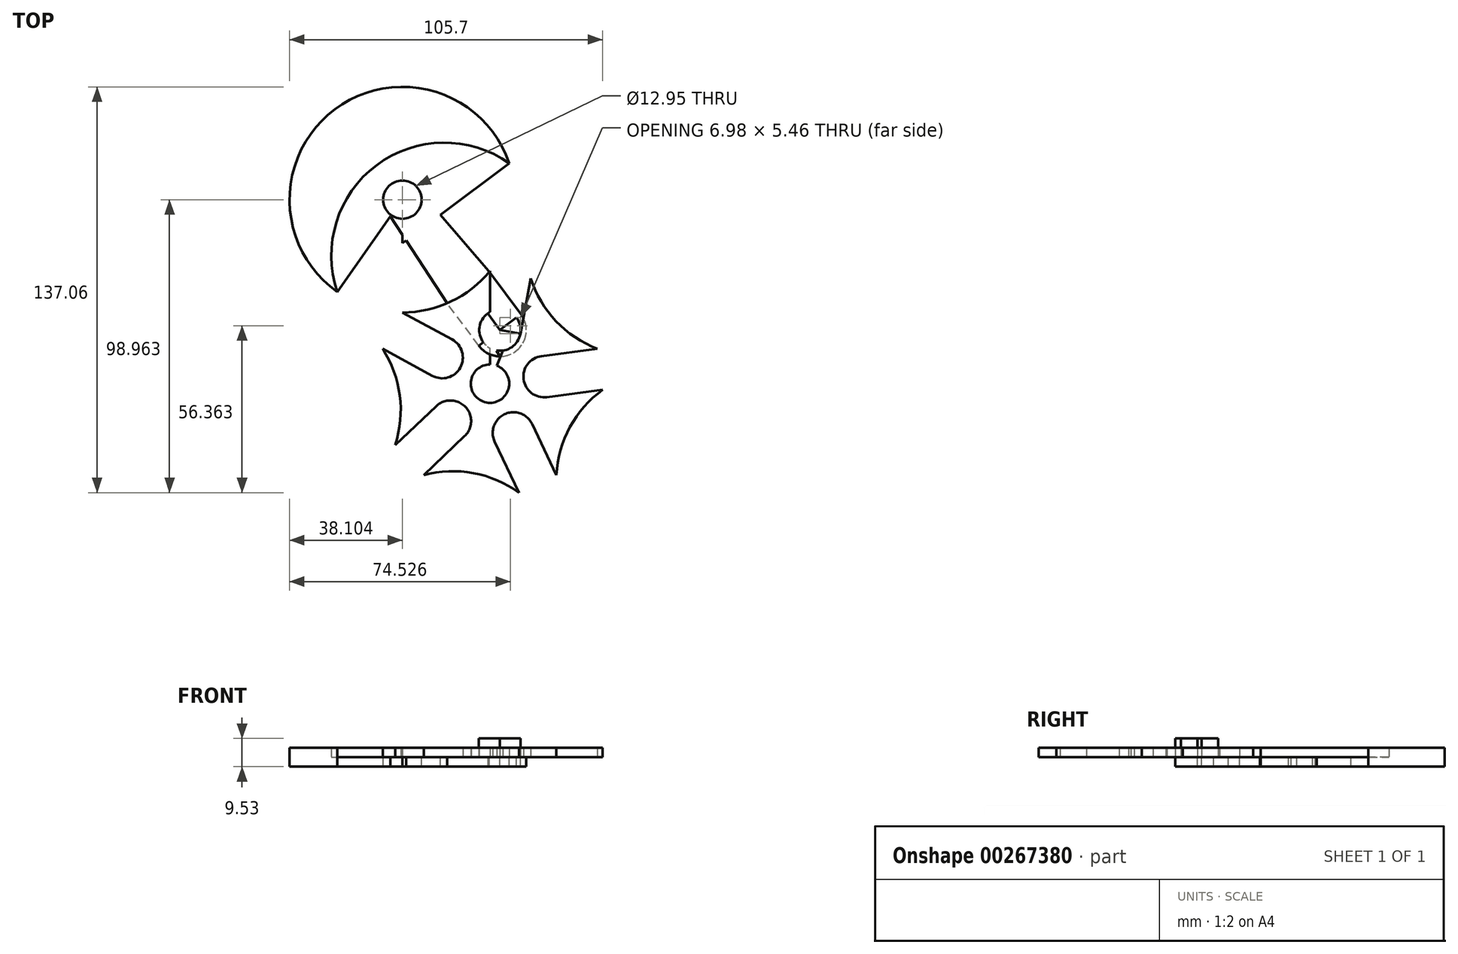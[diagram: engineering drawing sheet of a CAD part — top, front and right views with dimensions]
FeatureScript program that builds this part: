
annotation { "Feature Type Name" : "Feature", "Feature Type Description" : "" }
export const myFeature = defineFeature(function(context is Context, id is Id, definition is map)
    precondition{}
    {
        {
            var Q0;
            Q0=qCreatedBy(makeId("Top.planeOp"),FACE);
            var sketch = newSketch(context, id + "F0", { "sketchPlane" : qUnion([Q0])});
            skCircle(sketch, "E0", {"center": v(0, 0) * mm, "radius": 38.1 * mm});
            skLineSegment(sketch, "E1", {"start": v(0, 0) * mm, "end": v(0, 38.1) * mm});
            skLineSegment(sketch, "E2", {"start": v(0, 0) * mm, "end": v(-36.24, 11.77) * mm});
            skLineSegment(sketch, "E3", {"start": v(0, 0) * mm, "end": v(-22.4, -30.82) * mm});
            skLineSegment(sketch, "E4", {"start": v(-22.4, -30.82) * mm, "end": v(-32, -20.68) * mm});
            skLineSegment(sketch, "E5", {"start": v(-32, -20.68) * mm, "end": v(-18.17, -7.58) * mm});
            skLineSegment(sketch, "E6", {"start": v(-18.17, -7.58) * mm, "end": v(-8.56, -17.73) * mm});
            skLineSegment(sketch, "E7", {"start": v(-8.56, -17.73) * mm, "end": v(-22.4, -30.82) * mm});
            skCircle(sketch, "E8", {"center": v(-13.36, -12.65) * mm, "radius": 6.99 * mm});
            skLineSegment(sketch, "E9", {"start": v(-32, -20.68) * mm, "end": v(-36.24, 11.77) * mm});
            skArc(sketch, "E10.MirrorC", {"start": v(-36.24, 11.77) * mm, "mid": v(-30.46, -3.97) * mm, "end": v(-32, -20.68) * mm});
            skLineSegment(sketch, "E11", {"start": v(0, 0) * mm, "end": v(22.4, -30.82) * mm});
            skLineSegment(sketch, "E12", {"start": v(22.4, -30.82) * mm, "end": v(0, 0) * mm});
            skLineSegment(sketch, "E13", {"start": v(0, 0) * mm, "end": v(36.24, 11.77) * mm});
            skLineSegment(sketch, "E14", {"start": v(22.4, -30.82) * mm, "end": v(9.78, -36.82) * mm});
            skLineSegment(sketch, "E15", {"start": v(9.78, -36.82) * mm, "end": v(1.6, -19.62) * mm});
            skLineSegment(sketch, "E16", {"start": v(1.6, -19.62) * mm, "end": v(14.21, -13.62) * mm});
            skLineSegment(sketch, "E17", {"start": v(14.21, -13.62) * mm, "end": v(22.4, -30.82) * mm});
            skCircle(sketch, "E18", {"center": v(7.9, -16.62) * mm, "radius": 6.99 * mm});
            skPoint(sketch, "E19.trimOffspring.end.orphan", {"position": v(-7.55, 17.26) * mm});
            skPoint(sketch, "E20.center.orphan", {"position": v(-1.29, 18.31) * mm});
            skPoint(sketch, "E20.start.orphan", {"position": v(4.97, 19.37) * mm});
            skLineSegment(sketch, "E21", {"start": v(-36.24, 11.77) * mm, "end": v(-29.56, 24.04) * mm});
            skLineSegment(sketch, "E22", {"start": v(-29.56, 24.04) * mm, "end": v(-12.82, 14.93) * mm});
            skLineSegment(sketch, "E23", {"start": v(-29.56, 24.04) * mm, "end": v(0, 38.1) * mm});
            skArc(sketch, "E24.MirrorC", {"start": v(0, 38.1) * mm, "mid": v(-13.2, 27.74) * mm, "end": v(-29.56, 24.04) * mm});
            skLineSegment(sketch, "E25", {"start": v(0, 38.1) * mm, "end": v(13.73, 35.54) * mm});
            skLineSegment(sketch, "E26", {"start": v(13.73, 35.54) * mm, "end": v(0, 0) * mm});
            skLineSegment(sketch, "E27", {"start": v(13.73, 35.54) * mm, "end": v(10.24, 16.81) * mm});
            skLineSegment(sketch, "E28", {"start": v(10.24, 16.81) * mm, "end": v(-3.5, 19.37) * mm});
            skLineSegment(sketch, "E29", {"start": v(-3.5, 19.37) * mm, "end": v(0, 38.1) * mm});
            skCircle(sketch, "E30", {"center": v(3.37, 18.1) * mm, "radius": 6.99 * mm});
            skLineSegment(sketch, "E31", {"start": v(13.73, 35.54) * mm, "end": v(36.24, 11.77) * mm});
            skArc(sketch, "E32.MirrorC", {"start": v(36.24, 11.77) * mm, "mid": v(22.3, 21.12) * mm, "end": v(13.73, 35.54) * mm});
            skLineSegment(sketch, "E33", {"start": v(36.24, 11.77) * mm, "end": v(38.04, -2.08) * mm});
            skLineSegment(sketch, "E34", {"start": v(38.04, -2.08) * mm, "end": v(19.15, -4.54) * mm});
            skLineSegment(sketch, "E35", {"start": v(19.15, -4.54) * mm, "end": v(17.35, 9.3) * mm});
            skLineSegment(sketch, "E36", {"start": v(17.35, 9.3) * mm, "end": v(36.24, 11.77) * mm});
            skLineSegment(sketch, "E37", {"start": v(38.04, -2.08) * mm, "end": v(22.4, -30.82) * mm});
            skArc(sketch, "E38.MirrorC", {"start": v(22.4, -30.82) * mm, "mid": v(26.98, -14.69) * mm, "end": v(38.04, -2.08) * mm});
            skCircle(sketch, "E39", {"center": v(18.25, 2.38) * mm, "radius": 6.99 * mm});
            skLineSegment(sketch, "E40", {"start": v(-22.4, -30.82) * mm, "end": v(9.78, -36.82) * mm});
            skArc(sketch, "E41.MirrorC", {"start": v(-22.4, -30.82) * mm, "mid": v(-5.63, -30.2) * mm, "end": v(9.78, -36.82) * mm});
            skLineSegment(sketch, "E42", {"start": v(-36.24, 11.77) * mm, "end": v(-19.5, 2.66) * mm});
            skLineSegment(sketch, "E43", {"start": v(-12.82, 14.93) * mm, "end": v(-19.5, 2.66) * mm});
            skCircle(sketch, "E44", {"center": v(-16.16, 8.8) * mm, "radius": 6.99 * mm});
            skSolve(sketch);
        }
        {
            var Q0;
            {var subQ0=sQuery(id+"F0.wireOp",EDGE,"E22");Q0=makeQuery(id+"F0.imprint","IMPRINT",FACE,{"disambiguationData":[TD([[makeQuery(id+"F0.imprint","IMPRINT",EDGE,{"derivedFrom":subQ0}),1.0]])]});}
            var Q1;
            {var subQ0=sQuery(id+"F0.wireOp",EDGE,"E5");Q1=makeQuery(id+"F0.imprint","IMPRINT",FACE,{"disambiguationData":[TD([[makeQuery(id+"F0.imprint","IMPRINT",EDGE,{"derivedFrom":subQ0}),1.0]])]});}
            var Q2;
            {var subQ1=sQuery(id+"F0.wireOp",EDGE,"E7");Q2=makeQuery(id+"F0.imprint","IMPRINT",FACE,{"disambiguationData":[TD([[makeQuery(id+"F0.imprint","IMPRINT",EDGE,{"derivedFrom":subQ1}),1.0]])]});}
            var Q3;
            {var subQ1=sQuery(id+"F0.wireOp",EDGE,"E17");Q3=makeQuery(id+"F0.imprint","IMPRINT",FACE,{"disambiguationData":[TD([[makeQuery(id+"F0.imprint","IMPRINT",EDGE,{"derivedFrom":subQ1}),1.0]])]});}
            var Q4;
            {var subQ1=sQuery(id+"F0.wireOp",EDGE,"E27");Q4=makeQuery(id+"F0.imprint","IMPRINT",FACE,{"disambiguationData":[TD([[makeQuery(id+"F0.imprint","IMPRINT",EDGE,{"derivedFrom":subQ1}),1.0]])]});}
            var Q5;
            {var subQ1=sQuery(id+"F0.wireOp",EDGE,"E1");var subQ3=sQuery(id+"F0.wireOp",EDGE,"E30");var subQ4=makeQuery(id+"F0.imprint","INTERSECT",VERTEX,{"disambiguationData":[OD(0.0)],"derivedFrom":[subQ1,subQ3]});Q5=makeQuery(id+"F0.imprint","IMPRINT",FACE,{"disambiguationData":[TD([[makeQuery(id+"F0.imprint","IMPRINT",EDGE,{"disambiguationData":[TD([[subQ4,-1.0]])],"derivedFrom":subQ3}),-1.0]])]});}
            extrude(context, id + "F1", {"entities" : qUnion([Q0, Q1, Q2, Q3, Q4, Q5]), "depth" : 3.17 * mm});
        }
        {
            var Q0;
            Q0=qCreatedBy(makeId("Top.planeOp"),FACE);
            var sketch = newSketch(context, id + "F2", { "sketchPlane" : qUnion([Q0])});
            skCircle(sketch, "E45", {"center": v(0, 0) * mm, "radius": 38.1 * mm});
            skLineSegment(sketch, "E46", {"start": v(0, 38.1) * mm, "end": v(0, 0) * mm});
            skLineSegment(sketch, "E47", {"start": v(0, 38.1) * mm, "end": v(13.73, 35.54) * mm});
            skLineSegment(sketch, "E48", {"start": v(0, 38.1) * mm, "end": v(-3.5, 19.37) * mm});
            skLineSegment(sketch, "E49", {"start": v(13.73, 35.54) * mm, "end": v(10.24, 16.81) * mm});
            skLineSegment(sketch, "E50", {"start": v(10.24, 16.81) * mm, "end": v(-3.5, 19.37) * mm});
            skCircle(sketch, "E51", {"center": v(3.37, 18.1) * mm, "radius": 6.99 * mm});
            skLineSegment(sketch, "E52", {"start": v(0, 0) * mm, "end": v(-36.24, 11.77) * mm});
            skLineSegment(sketch, "E53", {"start": v(0, 0) * mm, "end": v(-29.56, 24.04) * mm});
            skLineSegment(sketch, "E54", {"start": v(-29.56, 24.04) * mm, "end": v(-36.24, 11.77) * mm});
            skLineSegment(sketch, "E55", {"start": v(0, 38.1) * mm, "end": v(-29.56, 24.04) * mm});
            skCircle(sketch, "E56.MirrorC", {"center": v(-29.56, 62.14) * mm, "radius": 38.1 * mm});
            skCircle(sketch, "E57", {"center": v(3.37, 18.1) * mm, "radius": 8.9 * mm});
            skLineSegment(sketch, "E58", {"start": v(3.37, 18.1) * mm, "end": v(-25.68, 56.96) * mm});
            skLineSegment(sketch, "E59", {"start": v(3.37, 18.1) * mm, "end": v(10.5, 23.42) * mm});
            skLineSegment(sketch, "E60", {"start": v(10.5, 23.42) * mm, "end": v(-3.75, 12.77) * mm});
            skLineSegment(sketch, "E61", {"start": v(-3.75, 12.77) * mm, "end": v(-14.5, 27.15) * mm});
            skLineSegment(sketch, "E62", {"start": v(10.5, 23.42) * mm, "end": v(-0.25, 37.8) * mm});
            skCircle(sketch, "E63", {"center": v(-29.56, 62.14) * mm, "radius": 6.48 * mm});
            skLineSegment(sketch, "E64", {"start": v(-0.25, 37.8) * mm, "end": v(-24.63, 66.35) * mm});
            skLineSegment(sketch, "E65", {"start": v(-14.5, 27.15) * mm, "end": v(-34.98, 58.6) * mm});
            skLineSegment(sketch, "E66", {"start": v(-34.98, 58.6) * mm, "end": v(-24.63, 66.35) * mm});
            skLineSegment(sketch, "E67", {"start": v(-29.56, 24.04) * mm, "end": v(-29.56, 62.14) * mm});
            skLineSegment(sketch, "E68", {"start": v(-29.56, 62.14) * mm, "end": v(6.52, 74.4) * mm});
            skLineSegment(sketch, "E69", {"start": v(-29.56, 62.14) * mm, "end": v(-51.53, 31.02) * mm});
            skLineSegment(sketch, "E70.trimOffspring", {"start": v(-0.62, 38.1) * mm, "end": v(-0.25, 37.8) * mm});
            skLineSegment(sketch, "E71", {"start": v(-25.68, 56.96) * mm, "end": v(-29.56, 62.14) * mm});
            skLineSegment(sketch, "E72", {"start": v(-51.53, 31.02) * mm, "end": v(6.52, 74.4) * mm});
            skArc(sketch, "E73.MirrorC", {"start": v(6.52, 74.4) * mm, "mid": v(-38.27, 73.8) * mm, "end": v(-51.53, 31.02) * mm});
            skLineSegment(sketch, "E74", {"start": v(-10.7, 33.01) * mm, "end": v(10.8, -3.44) * mm});
            skSolve(sketch);
        }
        {
            var Q0;
            {var subQ0=sQuery(id+"F2.wireOp",EDGE,"E51");var subQ1=sQuery(id+"F2.wireOp",EDGE,"E46");var subQ2=makeQuery(id+"F2.imprint","INTERSECT",VERTEX,{"disambiguationData":[OD(0.0)],"derivedFrom":[subQ1,subQ0]});Q0=makeQuery(id+"F2.imprint","IMPRINT",FACE,{"disambiguationData":[TD([[makeQuery(id+"F2.imprint","IMPRINT",EDGE,{"disambiguationData":[TD([[subQ2,-1.0]])],"derivedFrom":subQ1}),1.0]])]});}
            var Q1;
            {var subQ0=sQuery(id+"F2.wireOp",EDGE,"E51");var subQ3=sQuery(id+"F2.wireOp",EDGE,"E60");var subQ5=makeQuery(id+"F2.imprint","INTERSECT",VERTEX,{"disambiguationData":[OD(0.0)],"derivedFrom":[subQ0,subQ3]});Q1=makeQuery(id+"F2.imprint","IMPRINT",FACE,{"disambiguationData":[TD([[makeQuery(id+"F2.imprint","IMPRINT",EDGE,{"disambiguationData":[TD([[subQ5,1.0]])],"derivedFrom":subQ0}),1.0]])]});}
            var Q2;
            {var subQ0=sQuery(id+"F2.wireOp",EDGE,"E60");var subQ1=sQuery(id+"F2.wireOp",EDGE,"E46");var subQ2=makeQuery(id+"F2.imprint","INTERSECT",VERTEX,{"derivedFrom":[subQ1,subQ0]});Q2=makeQuery(id+"F2.imprint","IMPRINT",FACE,{"disambiguationData":[TD([[makeQuery(id+"F2.imprint","IMPRINT",EDGE,{"disambiguationData":[TD([[subQ2,-1.0]])],"derivedFrom":subQ1}),1.0]])]});}
            var Q3;
            {var subQ0=sQuery(id+"F2.wireOp",EDGE,"E50");var subQ1=sQuery(id+"F2.wireOp",EDGE,"E46");var subQ2=makeQuery(id+"F2.imprint","INTERSECT",VERTEX,{"derivedFrom":[subQ1,subQ0]});Q3=makeQuery(id+"F2.imprint","IMPRINT",FACE,{"disambiguationData":[TD([[makeQuery(id+"F2.imprint","IMPRINT",EDGE,{"disambiguationData":[TD([[subQ2,-1.0]])],"derivedFrom":subQ1}),-1.0]])]});}
            var Q4;
            {var subQ0=sQuery(id+"F2.wireOp",EDGE,"E50");var subQ1=sQuery(id+"F2.wireOp",EDGE,"E46");var subQ2=makeQuery(id+"F2.imprint","INTERSECT",VERTEX,{"derivedFrom":[subQ1,subQ0]});Q4=makeQuery(id+"F2.imprint","IMPRINT",FACE,{"disambiguationData":[TD([[makeQuery(id+"F2.imprint","IMPRINT",EDGE,{"disambiguationData":[TD([[subQ2,-1.0]])],"derivedFrom":subQ1}),1.0]])]});}
            var Q5;
            {var subQ0=sQuery(id+"F2.wireOp",EDGE,"E58");var subQ1=sQuery(id+"F2.wireOp",EDGE,"E46");var subQ2=makeQuery(id+"F2.imprint","INTERSECT",VERTEX,{"derivedFrom":[subQ1,subQ0]});Q5=makeQuery(id+"F2.imprint","IMPRINT",FACE,{"disambiguationData":[TD([[makeQuery(id+"F2.imprint","IMPRINT",EDGE,{"disambiguationData":[TD([[subQ2,-1.0]])],"derivedFrom":subQ1}),1.0]])]});}
            var Q6;
            {var subQ0=sQuery(id+"F2.wireOp",EDGE,"E51");var subQ1=sQuery(id+"F2.wireOp",EDGE,"E46");var subQ2=makeQuery(id+"F2.imprint","INTERSECT",VERTEX,{"disambiguationData":[OD(1.0)],"derivedFrom":[subQ1,subQ0]});Q6=makeQuery(id+"F2.imprint","IMPRINT",FACE,{"disambiguationData":[TD([[makeQuery(id+"F2.imprint","IMPRINT",EDGE,{"disambiguationData":[TD([[subQ2,-1.0]])],"derivedFrom":subQ1}),-1.0]])]});}
            var Q7;
            {var subQ1=sQuery(id+"F2.wireOp",EDGE,"E48");var subQ3=sQuery(id+"F2.wireOp",EDGE,"E57");var subQ4=makeQuery(id+"F2.imprint","INTERSECT",VERTEX,{"derivedFrom":[subQ1,subQ3]});Q7=makeQuery(id+"F2.imprint","IMPRINT",FACE,{"disambiguationData":[TD([[makeQuery(id+"F2.imprint","IMPRINT",EDGE,{"disambiguationData":[TD([[subQ4,-1.0]])],"derivedFrom":subQ1}),-1.0]])]});}
            var Q8;
            {var subQ0=sQuery(id+"F2.wireOp",EDGE,"E51");var subQ1=sQuery(id+"F2.wireOp",EDGE,"E46");var subQ2=makeQuery(id+"F2.imprint","INTERSECT",VERTEX,{"disambiguationData":[OD(1.0)],"derivedFrom":[subQ1,subQ0]});Q8=makeQuery(id+"F2.imprint","IMPRINT",FACE,{"disambiguationData":[TD([[makeQuery(id+"F2.imprint","IMPRINT",EDGE,{"disambiguationData":[TD([[subQ2,-1.0]])],"derivedFrom":subQ1}),1.0]])]});}
            var Q9;
            {var subQ1=sQuery(id+"F2.wireOp",EDGE,"E49");var subQ3=sQuery(id+"F2.wireOp",EDGE,"E57");var subQ4=makeQuery(id+"F2.imprint","INTERSECT",VERTEX,{"derivedFrom":[subQ1,subQ3]});Q9=makeQuery(id+"F2.imprint","IMPRINT",FACE,{"disambiguationData":[TD([[makeQuery(id+"F2.imprint","IMPRINT",EDGE,{"disambiguationData":[TD([[subQ4,-1.0]])],"derivedFrom":subQ1}),-1.0]])]});}
            var Q10;
            {var subQ0=sQuery(id+"F2.wireOp",EDGE,"E57");var subQ1=sQuery(id+"F2.wireOp",EDGE,"E46");var subQ2=makeQuery(id+"F2.imprint","INTERSECT",VERTEX,{"disambiguationData":[OD(0.0)],"derivedFrom":[subQ1,subQ0]});Q10=makeQuery(id+"F2.imprint","IMPRINT",FACE,{"disambiguationData":[TD([[makeQuery(id+"F2.imprint","IMPRINT",EDGE,{"disambiguationData":[TD([[subQ2,-1.0]])],"derivedFrom":subQ1}),1.0]])]});}
            var Q11;
            {var subQ0=sQuery(id+"F2.wireOp",EDGE,"E57");var subQ1=sQuery(id+"F2.wireOp",EDGE,"E46");var subQ2=makeQuery(id+"F2.imprint","INTERSECT",VERTEX,{"disambiguationData":[OD(0.0)],"derivedFrom":[subQ1,subQ0]});Q11=makeQuery(id+"F2.imprint","IMPRINT",FACE,{"disambiguationData":[TD([[makeQuery(id+"F2.imprint","IMPRINT",EDGE,{"disambiguationData":[TD([[subQ2,-1.0]])],"derivedFrom":subQ1}),-1.0]])]});}
            var Q12;
            {var subQ1=sQuery(id+"F2.wireOp",EDGE,"E48");var subQ3=sQuery(id+"F2.wireOp",EDGE,"E57");var subQ4=makeQuery(id+"F2.imprint","INTERSECT",VERTEX,{"derivedFrom":[subQ1,subQ3]});Q12=makeQuery(id+"F2.imprint","IMPRINT",FACE,{"disambiguationData":[TD([[makeQuery(id+"F2.imprint","IMPRINT",EDGE,{"disambiguationData":[TD([[subQ4,1.0]])],"derivedFrom":subQ3}),1.0]])]});}
            var Q13;
            {var subQ0=sQuery(id+"F2.wireOp",EDGE,"E61");Q13=makeQuery(id+"F2.imprint","IMPRINT",FACE,{"disambiguationData":[TD([[makeQuery(id+"F2.imprint","IMPRINT",EDGE,{"derivedFrom":subQ0}),-1.0]])]});}
            var Q14;
            {var subQ0=sQuery(id+"F2.wireOp",EDGE,"E62");var subQ1=sQuery(id+"F2.wireOp",EDGE,"E48");var subQ2=makeQuery(id+"F2.imprint","INTERSECT",VERTEX,{"derivedFrom":[subQ1,subQ0]});Q14=makeQuery(id+"F2.imprint","IMPRINT",FACE,{"disambiguationData":[TD([[makeQuery(id+"F2.imprint","IMPRINT",EDGE,{"disambiguationData":[TD([[subQ2,-1.0]])],"derivedFrom":subQ1}),-1.0]])]});}
            var Q15;
            {var subQ0=sQuery(id+"F2.wireOp",EDGE,"E62");var subQ1=sQuery(id+"F2.wireOp",EDGE,"E46");var subQ2=makeQuery(id+"F2.imprint","INTERSECT",VERTEX,{"derivedFrom":[subQ1,subQ0]});Q15=makeQuery(id+"F2.imprint","IMPRINT",FACE,{"disambiguationData":[TD([[makeQuery(id+"F2.imprint","IMPRINT",EDGE,{"disambiguationData":[TD([[subQ2,-1.0]])],"derivedFrom":subQ1}),1.0]])]});}
            var Q16;
            {var subQ5=sQuery(id+"F2.wireOp",EDGE,"E46");var subQ7=sQuery(id+"F2.wireOp",EDGE,"E62");var subQ8=makeQuery(id+"F2.imprint","INTERSECT",VERTEX,{"derivedFrom":[subQ5,subQ7]});Q16=makeQuery(id+"F2.imprint","IMPRINT",FACE,{"disambiguationData":[TD([[makeQuery(id+"F2.imprint","IMPRINT",EDGE,{"disambiguationData":[TD([[subQ8,-1.0]])],"derivedFrom":subQ5}),-1.0]])]});}
            var Q17;
            {var subQ0=sQuery(id+"F2.wireOp",EDGE,"E51");var subQ1=sQuery(id+"F2.wireOp",EDGE,"E46");var subQ2=makeQuery(id+"F2.imprint","INTERSECT",VERTEX,{"disambiguationData":[OD(0.0)],"derivedFrom":[subQ1,subQ0]});Q17=makeQuery(id+"F2.imprint","IMPRINT",FACE,{"disambiguationData":[TD([[makeQuery(id+"F2.imprint","IMPRINT",EDGE,{"disambiguationData":[TD([[subQ2,-1.0]])],"derivedFrom":subQ1}),-1.0]])]});}
            var Q18;
            {var subQ0=sQuery(id+"F2.wireOp",EDGE,"E58");var subQ1=sQuery(id+"F2.wireOp",EDGE,"E48");var subQ2=makeQuery(id+"F2.imprint","INTERSECT",VERTEX,{"derivedFrom":[subQ1,subQ0]});Q18=makeQuery(id+"F2.imprint","IMPRINT",FACE,{"disambiguationData":[TD([[makeQuery(id+"F2.imprint","IMPRINT",EDGE,{"disambiguationData":[TD([[subQ2,-1.0]])],"derivedFrom":subQ1}),1.0]])]});}
            var Q19;
            {var subQ0=sQuery(id+"F2.wireOp",EDGE,"E70.trimOffspring");var subQ1=sQuery(id+"F2.wireOp",EDGE,"E55");var subQ2=makeQuery(id+"F2.imprint","INTERSECT",VERTEX,{"derivedFrom":[subQ1,subQ0]});Q19=makeQuery(id+"F2.imprint","IMPRINT",FACE,{"disambiguationData":[TD([[makeQuery(id+"F2.imprint","IMPRINT",EDGE,{"disambiguationData":[TD([[subQ2,-1.0]])],"derivedFrom":subQ1}),1.0]])]});}
            var Q20;
            {var subQ0=sQuery(id+"F2.wireOp",EDGE,"E58");var subQ1=sQuery(id+"F2.wireOp",EDGE,"E55");var subQ2=makeQuery(id+"F2.imprint","INTERSECT",VERTEX,{"derivedFrom":[subQ1,subQ0]});Q20=makeQuery(id+"F2.imprint","IMPRINT",FACE,{"disambiguationData":[TD([[makeQuery(id+"F2.imprint","IMPRINT",EDGE,{"disambiguationData":[TD([[subQ2,-1.0]])],"derivedFrom":subQ1}),1.0]])]});}
            var Q21;
            {var subQ0=sQuery(id+"F2.wireOp",EDGE,"E58");var subQ1=sQuery(id+"F2.wireOp",EDGE,"E45");var subQ2=makeQuery(id+"F2.imprint","INTERSECT",VERTEX,{"derivedFrom":[subQ1,subQ0]});Q21=makeQuery(id+"F2.imprint","IMPRINT",FACE,{"disambiguationData":[TD([[makeQuery(id+"F2.imprint","IMPRINT",EDGE,{"disambiguationData":[TD([[subQ2,-1.0]])],"derivedFrom":subQ1}),1.0]])]});}
            var Q22;
            {var subQ0=sQuery(id+"F2.wireOp",EDGE,"E70.trimOffspring");var subQ1=sQuery(id+"F2.wireOp",EDGE,"E45");var subQ2=makeQuery(id+"F2.imprint","INTERSECT",VERTEX,{"derivedFrom":[subQ1,subQ0]});Q22=makeQuery(id+"F2.imprint","IMPRINT",FACE,{"disambiguationData":[TD([[makeQuery(id+"F2.imprint","IMPRINT",EDGE,{"disambiguationData":[TD([[subQ2,-1.0]])],"derivedFrom":subQ1}),1.0]])]});}
            var Q23;
            {var subQ1=sQuery(id+"F2.wireOp",EDGE,"E45");var subQ8=makeQuery(id+"F2.imprint","INTERSECT",VERTEX,{"derivedFrom":[subQ1,sQuery(id+"F2.wireOp",EDGE,"E70.trimOffspring")]});Q23=makeQuery(id+"F2.imprint","IMPRINT",FACE,{"disambiguationData":[TD([[makeQuery(id+"F2.imprint","IMPRINT",EDGE,{"disambiguationData":[TD([[subQ8,1.0]])],"derivedFrom":subQ1}),-1.0]])]});}
            var Q24;
            {var subQ1=sQuery(id+"F2.wireOp",EDGE,"E45");var subQ5=sQuery(id+"F2.wireOp",EDGE,"E58");var subQ6=makeQuery(id+"F2.imprint","INTERSECT",VERTEX,{"derivedFrom":[subQ1,subQ5]});Q24=makeQuery(id+"F2.imprint","IMPRINT",FACE,{"disambiguationData":[TD([[makeQuery(id+"F2.imprint","IMPRINT",EDGE,{"disambiguationData":[TD([[subQ6,-1.0]])],"derivedFrom":subQ1}),-1.0]])]});}
            var Q25;
            {var subQ3=sQuery(id+"F2.wireOp",EDGE,"E64");var subQ5=sQuery(id+"F2.wireOp",EDGE,"E72");var subQ8=makeQuery(id+"F2.imprint","INTERSECT",VERTEX,{"derivedFrom":[subQ3,subQ5]});Q25=makeQuery(id+"F2.imprint","IMPRINT",FACE,{"disambiguationData":[TD([[makeQuery(id+"F2.imprint","IMPRINT",EDGE,{"disambiguationData":[TD([[subQ8,-1.0]])],"derivedFrom":subQ3}),1.0]])]});}
            var Q26;
            {var subQ0=sQuery(id+"F2.wireOp",EDGE,"E63");var subQ5=sQuery(id+"F2.wireOp",EDGE,"E67");var subQ6=makeQuery(id+"F2.imprint","INTERSECT",VERTEX,{"derivedFrom":[subQ0,subQ5]});Q26=makeQuery(id+"F2.imprint","IMPRINT",FACE,{"disambiguationData":[TD([[makeQuery(id+"F2.imprint","IMPRINT",EDGE,{"disambiguationData":[TD([[subQ6,1.0]])],"derivedFrom":subQ5}),-1.0]])]});}
            var Q27;
            {var subQ0=sQuery(id+"F2.wireOp",EDGE,"E69");var subQ1=sQuery(id+"F2.wireOp",EDGE,"E63");var subQ2=makeQuery(id+"F2.imprint","INTERSECT",VERTEX,{"derivedFrom":[subQ1,subQ0]});Q27=makeQuery(id+"F2.imprint","IMPRINT",FACE,{"disambiguationData":[TD([[makeQuery(id+"F2.imprint","IMPRINT",EDGE,{"disambiguationData":[TD([[subQ2,-1.0]])],"derivedFrom":subQ1}),-1.0]])]});}
            var Q28;
            {var subQ0=sQuery(id+"F2.wireOp",EDGE,"E69");var subQ1=sQuery(id+"F2.wireOp",EDGE,"E63");var subQ2=makeQuery(id+"F2.imprint","INTERSECT",VERTEX,{"derivedFrom":[subQ1,subQ0]});Q28=makeQuery(id+"F2.imprint","IMPRINT",FACE,{"disambiguationData":[TD([[makeQuery(id+"F2.imprint","IMPRINT",EDGE,{"disambiguationData":[TD([[subQ2,-1.0]])],"derivedFrom":subQ1}),1.0]])]});}
            var Q29;
            {var subQ0=sQuery(id+"F2.wireOp",EDGE,"E71");Q29=makeQuery(id+"F2.imprint","IMPRINT",FACE,{"disambiguationData":[TD([[makeQuery(id+"F2.imprint","IMPRINT",EDGE,{"derivedFrom":subQ0}),1.0]])]});}
            var Q30;
            {var subQ0=sQuery(id+"F2.wireOp",EDGE,"E71");Q30=makeQuery(id+"F2.imprint","IMPRINT",FACE,{"disambiguationData":[TD([[makeQuery(id+"F2.imprint","IMPRINT",EDGE,{"derivedFrom":subQ0}),-1.0]])]});}
            var Q31;
            {var subQ0=sQuery(id+"F2.wireOp",EDGE,"E66");var subQ1=sQuery(id+"F2.wireOp",EDGE,"E63");var subQ2=makeQuery(id+"F2.imprint","INTERSECT",VERTEX,{"derivedFrom":[subQ1,sQuery(id+"F2.wireOp",EDGE,"E64"),subQ0]});Q31=makeQuery(id+"F2.imprint","IMPRINT",FACE,{"disambiguationData":[TD([[makeQuery(id+"F2.imprint","IMPRINT",EDGE,{"disambiguationData":[TD([[subQ2,-1.0]])],"derivedFrom":subQ1}),1.0]])]});}
            var Q32;
            {var subQ1=sQuery(id+"F2.wireOp",EDGE,"E63");var subQ3=sQuery(id+"F2.wireOp",EDGE,"E69");var subQ4=makeQuery(id+"F2.imprint","INTERSECT",VERTEX,{"derivedFrom":[subQ1,subQ3]});Q32=makeQuery(id+"F2.imprint","IMPRINT",FACE,{"disambiguationData":[TD([[makeQuery(id+"F2.imprint","IMPRINT",EDGE,{"disambiguationData":[TD([[subQ4,1.0]])],"derivedFrom":subQ1}),1.0]])]});}
            var Q33;
            {var subQ1=sQuery(id+"F2.wireOp",EDGE,"E63");var subQ3=sQuery(id+"F2.wireOp",EDGE,"E69");var subQ4=makeQuery(id+"F2.imprint","INTERSECT",VERTEX,{"derivedFrom":[subQ1,subQ3]});Q33=makeQuery(id+"F2.imprint","IMPRINT",FACE,{"disambiguationData":[TD([[makeQuery(id+"F2.imprint","IMPRINT",EDGE,{"disambiguationData":[TD([[subQ4,-1.0]])],"derivedFrom":subQ3}),-1.0]])]});}
            var Q34;
            {var subQ1=sQuery(id+"F2.wireOp",EDGE,"E63");var subQ3=sQuery(id+"F2.wireOp",EDGE,"E68");var subQ4=makeQuery(id+"F2.imprint","INTERSECT",VERTEX,{"derivedFrom":[subQ1,subQ3]});Q34=makeQuery(id+"F2.imprint","IMPRINT",FACE,{"disambiguationData":[TD([[makeQuery(id+"F2.imprint","IMPRINT",EDGE,{"disambiguationData":[TD([[subQ4,-1.0]])],"derivedFrom":subQ1}),1.0]])]});}
            var Q35;
            {var subQ1=sQuery(id+"F2.wireOp",EDGE,"E63");var subQ3=sQuery(id+"F2.wireOp",EDGE,"E68");var subQ4=makeQuery(id+"F2.imprint","INTERSECT",VERTEX,{"derivedFrom":[subQ1,subQ3]});Q35=makeQuery(id+"F2.imprint","IMPRINT",FACE,{"disambiguationData":[TD([[makeQuery(id+"F2.imprint","IMPRINT",EDGE,{"disambiguationData":[TD([[subQ4,-1.0]])],"derivedFrom":subQ3}),1.0]])]});}
            var Q36;
            {var subQ0=sQuery(id+"F2.wireOp",EDGE,"E73.MirrorC");Q36=makeQuery(id+"F2.imprint","IMPRINT",FACE,{"disambiguationData":[TD([[makeQuery(id+"F2.imprint","IMPRINT",EDGE,{"derivedFrom":subQ0}),-1.0]])]});}
            var Q37;
            {var subQ0=sQuery(id+"F2.wireOp",EDGE,"E73.MirrorC");Q37=makeQuery(id+"F2.imprint","IMPRINT",FACE,{"disambiguationData":[TD([[makeQuery(id+"F2.imprint","IMPRINT",EDGE,{"derivedFrom":subQ0}),1.0]])]});}
            var Q38;
            {var subQ0=sQuery(id+"F2.wireOp",EDGE,"E72");var subQ1=sQuery(id+"F2.wireOp",EDGE,"E65");var subQ2=makeQuery(id+"F2.imprint","INTERSECT",VERTEX,{"derivedFrom":[subQ1,subQ0]});Q38=makeQuery(id+"F2.imprint","IMPRINT",FACE,{"disambiguationData":[TD([[makeQuery(id+"F2.imprint","IMPRINT",EDGE,{"disambiguationData":[TD([[subQ2,-1.0]])],"derivedFrom":subQ1}),1.0]])]});}
            var Q39;
            {var subQ0=sQuery(id+"F2.wireOp",EDGE,"E72");var subQ1=sQuery(id+"F2.wireOp",EDGE,"E64");var subQ2=makeQuery(id+"F2.imprint","INTERSECT",VERTEX,{"derivedFrom":[subQ1,subQ0]});Q39=makeQuery(id+"F2.imprint","IMPRINT",FACE,{"disambiguationData":[TD([[makeQuery(id+"F2.imprint","IMPRINT",EDGE,{"disambiguationData":[TD([[subQ2,-1.0]])],"derivedFrom":subQ1}),-1.0]])]});}
            var Q40;
            {var subQ5=sQuery(id+"F2.wireOp",EDGE,"E74");var subQ7=sQuery(id+"F2.wireOp",EDGE,"E48");var subQ9=makeQuery(id+"F2.imprint","INTERSECT",VERTEX,{"derivedFrom":[subQ7,subQ5]});Q40=makeQuery(id+"F2.imprint","IMPRINT",FACE,{"disambiguationData":[TD([[makeQuery(id+"F2.imprint","IMPRINT",EDGE,{"disambiguationData":[TD([[subQ9,1.0]])],"derivedFrom":subQ5}),-1.0]])]});}
            var Q41;
            {var subQ0=sQuery(id+"F2.wireOp",EDGE,"E51");var subQ5=sQuery(id+"F2.wireOp",EDGE,"E60");var subQ6=makeQuery(id+"F2.imprint","INTERSECT",VERTEX,{"disambiguationData":[OD(1.0)],"derivedFrom":[subQ0,subQ5]});Q41=makeQuery(id+"F2.imprint","IMPRINT",FACE,{"disambiguationData":[TD([[makeQuery(id+"F2.imprint","IMPRINT",EDGE,{"disambiguationData":[TD([[subQ6,1.0]])],"derivedFrom":subQ5}),-1.0]])]});}
            var Q42;
            {var subQ0=sQuery(id+"F2.wireOp",EDGE,"E74");var subQ1=sQuery(id+"F2.wireOp",EDGE,"E46");var subQ2=makeQuery(id+"F2.imprint","INTERSECT",VERTEX,{"derivedFrom":[subQ1,subQ0]});Q42=makeQuery(id+"F2.imprint","IMPRINT",FACE,{"disambiguationData":[TD([[makeQuery(id+"F2.imprint","IMPRINT",EDGE,{"disambiguationData":[TD([[subQ2,-1.0]])],"derivedFrom":subQ1}),1.0]])]});}
            var Q43;
            {var subQ0=sQuery(id+"F2.wireOp",EDGE,"E74");var subQ1=sQuery(id+"F2.wireOp",EDGE,"E46");var subQ2=makeQuery(id+"F2.imprint","INTERSECT",VERTEX,{"derivedFrom":[subQ1,subQ0]});Q43=makeQuery(id+"F2.imprint","IMPRINT",FACE,{"disambiguationData":[TD([[makeQuery(id+"F2.imprint","IMPRINT",EDGE,{"disambiguationData":[TD([[subQ2,-1.0]])],"derivedFrom":subQ1}),-1.0]])]});}
            var Q44;
            {var subQ0=sQuery(id+"F2.wireOp",EDGE,"E58");var subQ5=sQuery(id+"F2.wireOp",EDGE,"E46");var subQ6=makeQuery(id+"F2.imprint","INTERSECT",VERTEX,{"derivedFrom":[subQ5,subQ0]});Q44=makeQuery(id+"F2.imprint","IMPRINT",FACE,{"disambiguationData":[TD([[makeQuery(id+"F2.imprint","IMPRINT",EDGE,{"disambiguationData":[TD([[subQ6,-1.0]])],"derivedFrom":subQ5}),-1.0]])]});}
            var Q45;
            {var subQ1=sQuery(id+"F2.wireOp",EDGE,"E50");var subQ3=sQuery(id+"F2.wireOp",EDGE,"E74");var subQ4=makeQuery(id+"F2.imprint","INTERSECT",VERTEX,{"derivedFrom":[subQ1,subQ3]});Q45=makeQuery(id+"F2.imprint","IMPRINT",FACE,{"disambiguationData":[TD([[makeQuery(id+"F2.imprint","IMPRINT",EDGE,{"disambiguationData":[TD([[subQ4,1.0]])],"derivedFrom":subQ3}),-1.0]])]});}
            var Q46;
            {var subQ0=sQuery(id+"F2.wireOp",EDGE,"E60");var subQ1=sQuery(id+"F2.wireOp",EDGE,"E46");var subQ2=makeQuery(id+"F2.imprint","INTERSECT",VERTEX,{"derivedFrom":[subQ1,subQ0]});Q46=makeQuery(id+"F2.imprint","IMPRINT",FACE,{"disambiguationData":[TD([[makeQuery(id+"F2.imprint","IMPRINT",EDGE,{"disambiguationData":[TD([[subQ2,-1.0]])],"derivedFrom":subQ1}),-1.0]])]});}
            var Q47;
            {var subQ3=sQuery(id+"F2.wireOp",EDGE,"E57");var subQ5=sQuery(id+"F2.wireOp",EDGE,"E74");var subQ6=makeQuery(id+"F2.imprint","INTERSECT",VERTEX,{"disambiguationData":[OD(0.0)],"derivedFrom":[subQ3,subQ5]});Q47=makeQuery(id+"F2.imprint","IMPRINT",FACE,{"disambiguationData":[TD([[makeQuery(id+"F2.imprint","IMPRINT",EDGE,{"disambiguationData":[TD([[subQ6,-1.0]])],"derivedFrom":subQ3}),1.0]])]});}
            var Q48;
            {var subQ0=sQuery(id+"F2.wireOp",EDGE,"E58");var subQ1=sQuery(id+"F2.wireOp",EDGE,"E48");var subQ2=makeQuery(id+"F2.imprint","INTERSECT",VERTEX,{"derivedFrom":[subQ1,subQ0]});Q48=makeQuery(id+"F2.imprint","IMPRINT",FACE,{"disambiguationData":[TD([[makeQuery(id+"F2.imprint","IMPRINT",EDGE,{"disambiguationData":[TD([[subQ2,-1.0]])],"derivedFrom":subQ1}),-1.0]])]});}
            var Q49;
            {var subQ0=sQuery(id+"F2.wireOp",EDGE,"E74");var subQ1=sQuery(id+"F2.wireOp",EDGE,"E55");var subQ2=makeQuery(id+"F2.imprint","INTERSECT",VERTEX,{"derivedFrom":[subQ1,subQ0]});Q49=makeQuery(id+"F2.imprint","IMPRINT",FACE,{"disambiguationData":[TD([[makeQuery(id+"F2.imprint","IMPRINT",EDGE,{"disambiguationData":[TD([[subQ2,-1.0]])],"derivedFrom":subQ1}),1.0]])]});}
            var Q50;
            {var subQ1=sQuery(id+"F2.wireOp",EDGE,"E48");var subQ3=sQuery(id+"F2.wireOp",EDGE,"E74");var subQ4=makeQuery(id+"F2.imprint","INTERSECT",VERTEX,{"derivedFrom":[subQ1,subQ3]});Q50=makeQuery(id+"F2.imprint","IMPRINT",FACE,{"disambiguationData":[TD([[makeQuery(id+"F2.imprint","IMPRINT",EDGE,{"disambiguationData":[TD([[subQ4,-1.0]])],"derivedFrom":subQ3}),-1.0]])]});}
            extrude(context, id + "F3", {"entities" : qUnion([Q0, Q1, Q2, Q3, Q4, Q5, Q6, Q7, Q8, Q9, Q10, Q11, Q12, Q13, Q14, Q15, Q16, Q17, Q18, Q19, Q20, Q21, Q22, Q23, Q24, Q25, Q26, Q27, Q28, Q29, Q30, Q31, Q32, Q33, Q34, Q35, Q36, Q37, Q38, Q39, Q40, Q41, Q42, Q43, Q44, Q45, Q46, Q47, Q48, Q49, Q50]), "oppositeDirection" : true, "depth" : 3.17 * mm});
        }
        {
            var Q0;
            {var subQ0=sQuery(id+"F2.wireOp",EDGE,"E73.MirrorC");Q0=makeQuery(id+"F2.imprint","IMPRINT",FACE,{"disambiguationData":[TD([[makeQuery(id+"F2.imprint","IMPRINT",EDGE,{"derivedFrom":subQ0}),-1.0]])]});}
            extrude(context, id + "F4", {"entities" : qUnion([Q0]), "operationType" : NewBodyOperationType.ADD, "depth" : 3.17 * mm});
        }
        {
            var Q0;
            {var subQ0=sQuery(id+"F2.wireOp",EDGE,"E51");var subQ1=sQuery(id+"F2.wireOp",EDGE,"E46");var subQ2=makeQuery(id+"F2.imprint","INTERSECT",VERTEX,{"disambiguationData":[OD(0.0)],"derivedFrom":[subQ1,subQ0]});Q0=makeQuery(id+"F2.imprint","IMPRINT",FACE,{"disambiguationData":[TD([[makeQuery(id+"F2.imprint","IMPRINT",EDGE,{"disambiguationData":[TD([[subQ2,-1.0]])],"derivedFrom":subQ1}),1.0]])]});}
            var Q1;
            {var subQ0=sQuery(id+"F2.wireOp",EDGE,"E51");var subQ3=sQuery(id+"F2.wireOp",EDGE,"E60");var subQ5=makeQuery(id+"F2.imprint","INTERSECT",VERTEX,{"disambiguationData":[OD(0.0)],"derivedFrom":[subQ0,subQ3]});Q1=makeQuery(id+"F2.imprint","IMPRINT",FACE,{"disambiguationData":[TD([[makeQuery(id+"F2.imprint","IMPRINT",EDGE,{"disambiguationData":[TD([[subQ5,1.0]])],"derivedFrom":subQ0}),1.0]])]});}
            var Q2;
            {var subQ0=sQuery(id+"F2.wireOp",EDGE,"E60");var subQ1=sQuery(id+"F2.wireOp",EDGE,"E46");var subQ2=makeQuery(id+"F2.imprint","INTERSECT",VERTEX,{"derivedFrom":[subQ1,subQ0]});Q2=makeQuery(id+"F2.imprint","IMPRINT",FACE,{"disambiguationData":[TD([[makeQuery(id+"F2.imprint","IMPRINT",EDGE,{"disambiguationData":[TD([[subQ2,-1.0]])],"derivedFrom":subQ1}),1.0]])]});}
            var Q3;
            {var subQ0=sQuery(id+"F2.wireOp",EDGE,"E58");var subQ1=sQuery(id+"F2.wireOp",EDGE,"E46");var subQ2=makeQuery(id+"F2.imprint","INTERSECT",VERTEX,{"derivedFrom":[subQ1,subQ0]});Q3=makeQuery(id+"F2.imprint","IMPRINT",FACE,{"disambiguationData":[TD([[makeQuery(id+"F2.imprint","IMPRINT",EDGE,{"disambiguationData":[TD([[subQ2,-1.0]])],"derivedFrom":subQ1}),1.0]])]});}
            var Q4;
            {var subQ0=sQuery(id+"F2.wireOp",EDGE,"E50");var subQ1=sQuery(id+"F2.wireOp",EDGE,"E46");var subQ2=makeQuery(id+"F2.imprint","INTERSECT",VERTEX,{"derivedFrom":[subQ1,subQ0]});Q4=makeQuery(id+"F2.imprint","IMPRINT",FACE,{"disambiguationData":[TD([[makeQuery(id+"F2.imprint","IMPRINT",EDGE,{"disambiguationData":[TD([[subQ2,-1.0]])],"derivedFrom":subQ1}),1.0]])]});}
            var Q5;
            {var subQ0=sQuery(id+"F2.wireOp",EDGE,"E50");var subQ1=sQuery(id+"F2.wireOp",EDGE,"E46");var subQ2=makeQuery(id+"F2.imprint","INTERSECT",VERTEX,{"derivedFrom":[subQ1,subQ0]});Q5=makeQuery(id+"F2.imprint","IMPRINT",FACE,{"disambiguationData":[TD([[makeQuery(id+"F2.imprint","IMPRINT",EDGE,{"disambiguationData":[TD([[subQ2,-1.0]])],"derivedFrom":subQ1}),-1.0]])]});}
            var Q6;
            {var subQ0=sQuery(id+"F2.wireOp",EDGE,"E58");var subQ1=sQuery(id+"F2.wireOp",EDGE,"E46");var subQ2=makeQuery(id+"F2.imprint","INTERSECT",VERTEX,{"derivedFrom":[subQ1,subQ0]});Q6=makeQuery(id+"F2.imprint","IMPRINT",FACE,{"disambiguationData":[TD([[makeQuery(id+"F2.imprint","IMPRINT",EDGE,{"disambiguationData":[TD([[subQ2,-1.0]])],"derivedFrom":subQ1}),-1.0]])]});}
            var Q7;
            {var subQ0=sQuery(id+"F2.wireOp",EDGE,"E51");var subQ1=sQuery(id+"F2.wireOp",EDGE,"E46");var subQ2=makeQuery(id+"F2.imprint","INTERSECT",VERTEX,{"disambiguationData":[OD(0.0)],"derivedFrom":[subQ1,subQ0]});Q7=makeQuery(id+"F2.imprint","IMPRINT",FACE,{"disambiguationData":[TD([[makeQuery(id+"F2.imprint","IMPRINT",EDGE,{"disambiguationData":[TD([[subQ2,-1.0]])],"derivedFrom":subQ1}),-1.0]])]});}
            var Q8;
            {var subQ0=sQuery(id+"F2.wireOp",EDGE,"E60");var subQ1=sQuery(id+"F2.wireOp",EDGE,"E46");var subQ2=makeQuery(id+"F2.imprint","INTERSECT",VERTEX,{"derivedFrom":[subQ1,subQ0]});Q8=makeQuery(id+"F2.imprint","IMPRINT",FACE,{"disambiguationData":[TD([[makeQuery(id+"F2.imprint","IMPRINT",EDGE,{"disambiguationData":[TD([[subQ2,-1.0]])],"derivedFrom":subQ1}),-1.0]])]});}
            var Q9;
            {var subQ0=sQuery(id+"F2.wireOp",EDGE,"E51");var subQ5=sQuery(id+"F2.wireOp",EDGE,"E60");var subQ6=makeQuery(id+"F2.imprint","INTERSECT",VERTEX,{"disambiguationData":[OD(1.0)],"derivedFrom":[subQ0,subQ5]});Q9=makeQuery(id+"F2.imprint","IMPRINT",FACE,{"disambiguationData":[TD([[makeQuery(id+"F2.imprint","IMPRINT",EDGE,{"disambiguationData":[TD([[subQ6,1.0]])],"derivedFrom":subQ5}),-1.0]])]});}
            var Q10;
            {var subQ0=sQuery(id+"F2.wireOp",EDGE,"E74");var subQ1=sQuery(id+"F2.wireOp",EDGE,"E46");var subQ2=makeQuery(id+"F2.imprint","INTERSECT",VERTEX,{"derivedFrom":[subQ1,subQ0]});Q10=makeQuery(id+"F2.imprint","IMPRINT",FACE,{"disambiguationData":[TD([[makeQuery(id+"F2.imprint","IMPRINT",EDGE,{"disambiguationData":[TD([[subQ2,-1.0]])],"derivedFrom":subQ1}),-1.0]])]});}
            var Q11;
            {var subQ0=sQuery(id+"F2.wireOp",EDGE,"E74");var subQ1=sQuery(id+"F2.wireOp",EDGE,"E46");var subQ2=makeQuery(id+"F2.imprint","INTERSECT",VERTEX,{"derivedFrom":[subQ1,subQ0]});Q11=makeQuery(id+"F2.imprint","IMPRINT",FACE,{"disambiguationData":[TD([[makeQuery(id+"F2.imprint","IMPRINT",EDGE,{"disambiguationData":[TD([[subQ2,-1.0]])],"derivedFrom":subQ1}),1.0]])]});}
            var Q12;
            {var subQ1=sQuery(id+"F2.wireOp",EDGE,"E50");var subQ3=sQuery(id+"F2.wireOp",EDGE,"E74");var subQ4=makeQuery(id+"F2.imprint","INTERSECT",VERTEX,{"derivedFrom":[subQ1,subQ3]});Q12=makeQuery(id+"F2.imprint","IMPRINT",FACE,{"disambiguationData":[TD([[makeQuery(id+"F2.imprint","IMPRINT",EDGE,{"disambiguationData":[TD([[subQ4,1.0]])],"derivedFrom":subQ3}),-1.0]])]});}
            extrude(context, id + "F5", {"entities" : qUnion([Q0, Q1, Q2, Q3, Q4, Q5, Q6, Q7, Q8, Q9, Q10, Q11, Q12]), "depth" : 6.35 * mm});
        }
        {
            var Q0;
            Q0=sQuery(id+"F2.wireOp",VERTEX,"E53.start");
            var Q1;
            Q1=makeQuery(id+"F1.opExtrude","SWEPT_BODY",BODY,{"disambiguationData":[OSD([sQuery(id+"F0.wireOp",EDGE,"E5"),sQuery(id+"F0.wireOp",EDGE,"E7"),sQuery(id+"F0.wireOp",EDGE,"E8"),sQuery(id+"F0.wireOp",EDGE,"E10.MirrorC"),sQuery(id+"F0.wireOp",EDGE,"E15"),sQuery(id+"F0.wireOp",EDGE,"E17"),sQuery(id+"F0.wireOp",EDGE,"E18"),sQuery(id+"F0.wireOp",EDGE,"E22"),sQuery(id+"F0.wireOp",EDGE,"E24.MirrorC"),sQuery(id+"F0.wireOp",EDGE,"E27"),sQuery(id+"F0.wireOp",EDGE,"E29"),sQuery(id+"F0.wireOp",EDGE,"E30"),sQuery(id+"F0.wireOp",EDGE,"E32.MirrorC"),sQuery(id+"F0.wireOp",EDGE,"E34"),sQuery(id+"F0.wireOp",EDGE,"E36"),sQuery(id+"F0.wireOp",EDGE,"E38.MirrorC"),sQuery(id+"F0.wireOp",EDGE,"E39"),sQuery(id+"F0.wireOp",EDGE,"E41.MirrorC"),sQuery(id+"F0.wireOp",EDGE,"E42"),sQuery(id+"F0.wireOp",EDGE,"E44")])]});
            hole(context, id + "F6", {"style" : HoleStyle.SIMPLE, "endStyle" : HoleEndStyle.THROUGH, "oppositeDirection" : true, "holeDiameter" : 12.95 * mm, "tappedDepth" : 12.7 * mm, "tapClearance" : 3, "locations" : qUnion([Q0]), "scope" : qUnion([Q1])});
        }
        {
            var Q0;
            Q0=sQuery(id+"F2.wireOp",VERTEX,"E68.start");
            var Q1;
            Q1=makeQuery(id+"F3.opExtrude","SWEPT_BODY",BODY,{"disambiguationData":[OSD([sQuery(id+"F2.wireOp",EDGE,"E45"),sQuery(id+"F2.wireOp",EDGE,"E56.MirrorC"),sQuery(id+"F2.wireOp",EDGE,"E57"),sQuery(id+"F2.wireOp",EDGE,"E61"),sQuery(id+"F2.wireOp",EDGE,"E62"),sQuery(id+"F2.wireOp",EDGE,"E64"),sQuery(id+"F2.wireOp",EDGE,"E65"),sQuery(id+"F2.wireOp",EDGE,"E67"),sQuery(id+"F2.wireOp",EDGE,"E70.trimOffspring"),sQuery(id+"F2.wireOp",EDGE,"E72")])]});
            hole(context, id + "F7", {"style" : HoleStyle.SIMPLE, "endStyle" : HoleEndStyle.THROUGH, "holeDiameter" : 12.95 * mm, "tappedDepth" : 12.7 * mm, "tapClearance" : 3, "locations" : qUnion([Q0]), "scope" : qUnion([Q1])});
        }
    });
